# Revit family: SAFARI DL LED
name_source: partatom
category: Осветительные приборы
revit_build: Autodesk Revit 2016 (Build: 20150220_1215(x64)
units: mm (PartAtom-declared; Revit-internal decimal feet)

## family parameters
Источник света = Да
Общий = Нет
Основа = Грань
При загрузке вырезать с полостями = Нет
Размер круглого соединителя = Использовать диаметр
Тип детали = Нормальный
Точка расчета площади = Нет

## types (1)
- SAFARI DL LED
    ADSK_Единица измерения = Шт.
    ADSK_Завод-изготовитель = ООО МГК Световые технологии
    ADSK_Количество фаз = 1
    ADSK_Количество фаз числовое = 1
    ADSK_Коэффициент мощности = 0.92
    ADSK_Масса = 0
    ADSK_Наименование = Светодиодный светильник направленного света. Конструкция светильника делает возможным простой и легкий монтаж, а светодиодная COB матрица и фасетчатый отражатель обеспечивают яркое равномерное освещение.
    ADSK_Напряжение = 230 В
    ADSK_Номинальная мощность = 0 кВт
    ADSK_Полная мощность = 0 кВ·А
    ADSK_Размер_Высота = 68 мм
    ADSK_Размер_Радиус = 68 мм
    ADSK_Ток = 0 А
    ADSK_Энергоэффективность = 0 лм/Вт
    IP Class = IP44/IP20
    URL = http://ltcompany.com
    a = 8 мм
    b = 60 мм
    c = 58 мм
    d = 48 мм
    e = 15 мм
    Блок аварийного питания = Нет
    Видимая форма излучения при визуализации = Нет
    Группа модели = Светильники
    Изготовитель = ООО МГК Световые технологии
    Излучение по длине прямоугольника = 135 мм
    Излучение по ширине прямоугольника = 135 мм
    Климатическая зона = УХЛ4
    Код по классификатору = D5020200
    Корпус = Белый металл
    Область использования = Гипер-/супермаркеты, Гостиницы, Культурно-развлекательные, Магазины/Бутики, Объекты бытового обслуживания, Объекты общественного питания, ТРЦ
    Описание = Светодиодный светильник направленного света. Конструкция светильника делает возможным простой и легкий монтаж, а светодиодная COB матрица и фасетчатый отражатель обеспечивают яркое равномерное освещение.
    Отметка по умолчанию = 610 мм
    Плафон = Плафон самосвечение
    Полная установленная мощность = 0 кВ·А
    Разработчик = ООО ПРОРУБИМ
    Разработчик (телефон) = +7 (495) 649-85-43
    Светофильтр = 16777215
    Смещение цветовой температуры при затухании лампы = <Нет>
    Тип ИС = LED
    Тип продукции = Светильник
    Угол наклона = -90.00°
    Файл фотометрической сетки = generic
